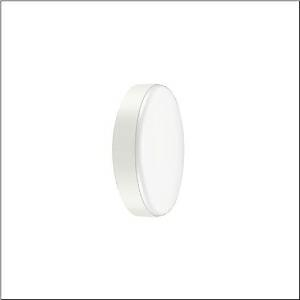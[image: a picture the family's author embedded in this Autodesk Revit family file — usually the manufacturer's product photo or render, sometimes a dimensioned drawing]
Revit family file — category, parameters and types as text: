
# Revit family: round_31_51wc10ma32as
name_source: partatom
category: Lighting Fixtures
units: mm (PartAtom-declared; Revit-internal decimal feet)

## family parameters
Cut with Voids When Loaded = No
Host = Face
Light Source = No
Part Type = Normal
Room Calculation Point = No
Round Connector Dimension = Use Diameter
Shared = No

## types (1)
- --- (1 x LED, 2450 lm, 20.4 W, 3000K)
    Apparent Load = 20 VA
    CIE Flux Codes = 44 75 94 94 100
    Color Rendering = 80
    Color Temperature = 3000K
    Default Elevation = 1800 mm
    Description = Round 31, wall and ceiling luminaire, primary optical cover: cover, of PC, opal, light emission: direct distribution, primary light characteristic: symmetric, installation type: surface-mounted, LED, rated luminous flux: 2.450lm, luminous efficacy: 120lm/W, light colour: 830, colour temperature: 3000K, control gear: ON/OFF Multilumen, with terminal, 3-pole, max. 2.5mm², mains connection: 220..240V, AC, 50/60Hz, rated input power: 20.5W, luminaire housing, of PC, traffic white (RAL 9016), diameter: 350mm, brightness and presence sensor, HF sensor, protection rating (complete): IP65, insulation class (complete): insulation class II (safety insulation), certification: CE, impact resistance: IK10, permissible operating ambient temperature: -20..+40°C, permissible storage temperature: -20..+60°C, packaging unit: 1 piece
    Height = 97 mm
    Lamp = 1 x LED
    Lamp Light Flux = 2450 lm
    Lamp Power = 20.4 W
    Lamp count = 1
    Length = 350 mm
    Luminous efficacy = 120 lm/W
    Manufacturer = Siteco
    ModVariant = No
    Model = 51WC10MA32AS
    Mounting Place = Ceiling
    Mounting Type = Surface mounted
    Number of Poles = 1
    OnlyDefault = Yes
    Power Factor = 1
    Product Name = Round 31
    Product group = wall and ceiling luminaire
    ProductGroupID = 304
    Protection Class = Protection class II
    Protection Degree = IP 65
    RLX_Detail_Level = 1
    RLX_Emergency_Light_Flux = 0 lm
    RLX_Emergency_Type = 0
    RLX_Emergency_Type_DB = No
    RlxData = <blob elided: 30253 chars, md5=d25a5145>
    Socket = socket
    Standby Power = 0 W
    System Light Flux = 2450 lm
    System Power = 20 W
    Type Comments = factory setting: luminous flux: 100 % | (ON | ON)
    Type Image = l_1007027.jpg
    URL = http://relux.com
    VarID = @adj_111858
    Voltage = 0 V
    Weight = 0.00 kg
    Width = 0 mm  [stored 0 ft]

note: [stored X ft] marks values corroborated as IEEE doubles in the binary element streams (Revit-internal decimal feet)

## geometry (parser evidence)
native form markers: Blend x4, Sweep x13
no freeform markers — native parametric forms only
